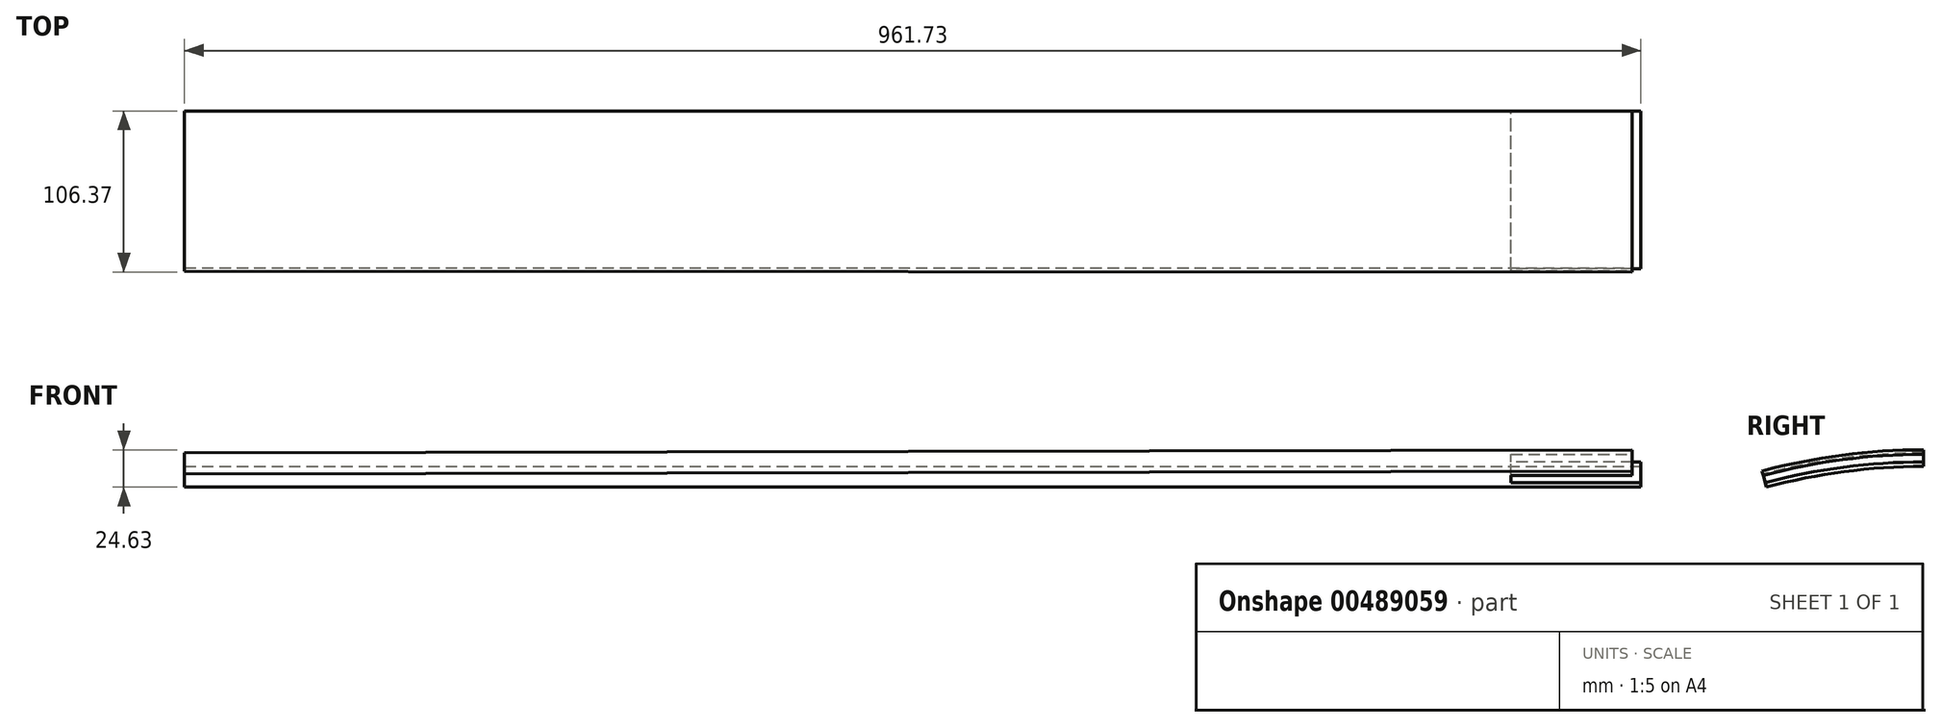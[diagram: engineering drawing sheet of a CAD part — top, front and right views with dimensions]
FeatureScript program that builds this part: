
annotation { "Feature Type Name" : "Feature", "Feature Type Description" : "" }
export const myFeature = defineFeature(function(context is Context, id is Id, definition is map)
    precondition{}
    {
        {
            var Q0;
            Q0=qCreatedBy(makeId("Front.planeOp"),FACE);
            var sketch = newSketch(context, id + "F0", { "sketchPlane" : qUnion([Q0])});
            skLineSegment(sketch, "E0", {"start": v(0, 0) * mm, "end": v(-1568.23, 0) * mm, "construction": true});
            skLineSegment(sketch, "E1", {"start": v(-1568.23, 0) * mm, "end": v(1340.07, 0) * mm, "construction": true});
            skLineSegment(sketch, "E2", {"start": v(0, 409) * mm, "end": v(0, 400) * mm});
            skLineSegment(sketch, "E3", {"start": v(0, 400) * mm, "end": v(961.73, 400) * mm});
            skLineSegment(sketch, "E4", {"start": v(961.73, 400) * mm, "end": v(961.73, 403) * mm});
            skLineSegment(sketch, "E5", {"start": v(961.73, 403) * mm, "end": v(875.96, 403) * mm});
            skLineSegment(sketch, "E6", {"start": v(875.96, 403) * mm, "end": v(875.96, 408) * mm});
            skLineSegment(sketch, "E7", {"start": v(875.96, 408) * mm, "end": v(955.96, 408) * mm});
            skLineSegment(sketch, "E8", {"start": v(955.96, 408) * mm, "end": v(955.96, 411) * mm});
            skLineSegment(sketch, "E9", {"start": v(955.96, 411) * mm, "end": v(0, 409) * mm});
            skSolve(sketch);
        }
        {
            var Q0;
            Q0=makeQuery(id+"F0.imprint","IMPRINT",FACE,{"disambiguationData":[TD([[makeQuery(id+"F0.imprint","IMPRINT",EDGE,{"derivedFrom":sQuery(id+"F0.wireOp",EDGE,"E2")}),1.0]])]});
            var Q1;
            Q1=sQuery(id+"F0.wireOp",EDGE,"E1");
            revolve(context, id + "F1", {"entities" : qUnion([Q0]), "axis" : qUnion([Q1]), "revolveType" : RevolveType.ONE_DIRECTION, "angle" : 15 * degree});
        }
    });
